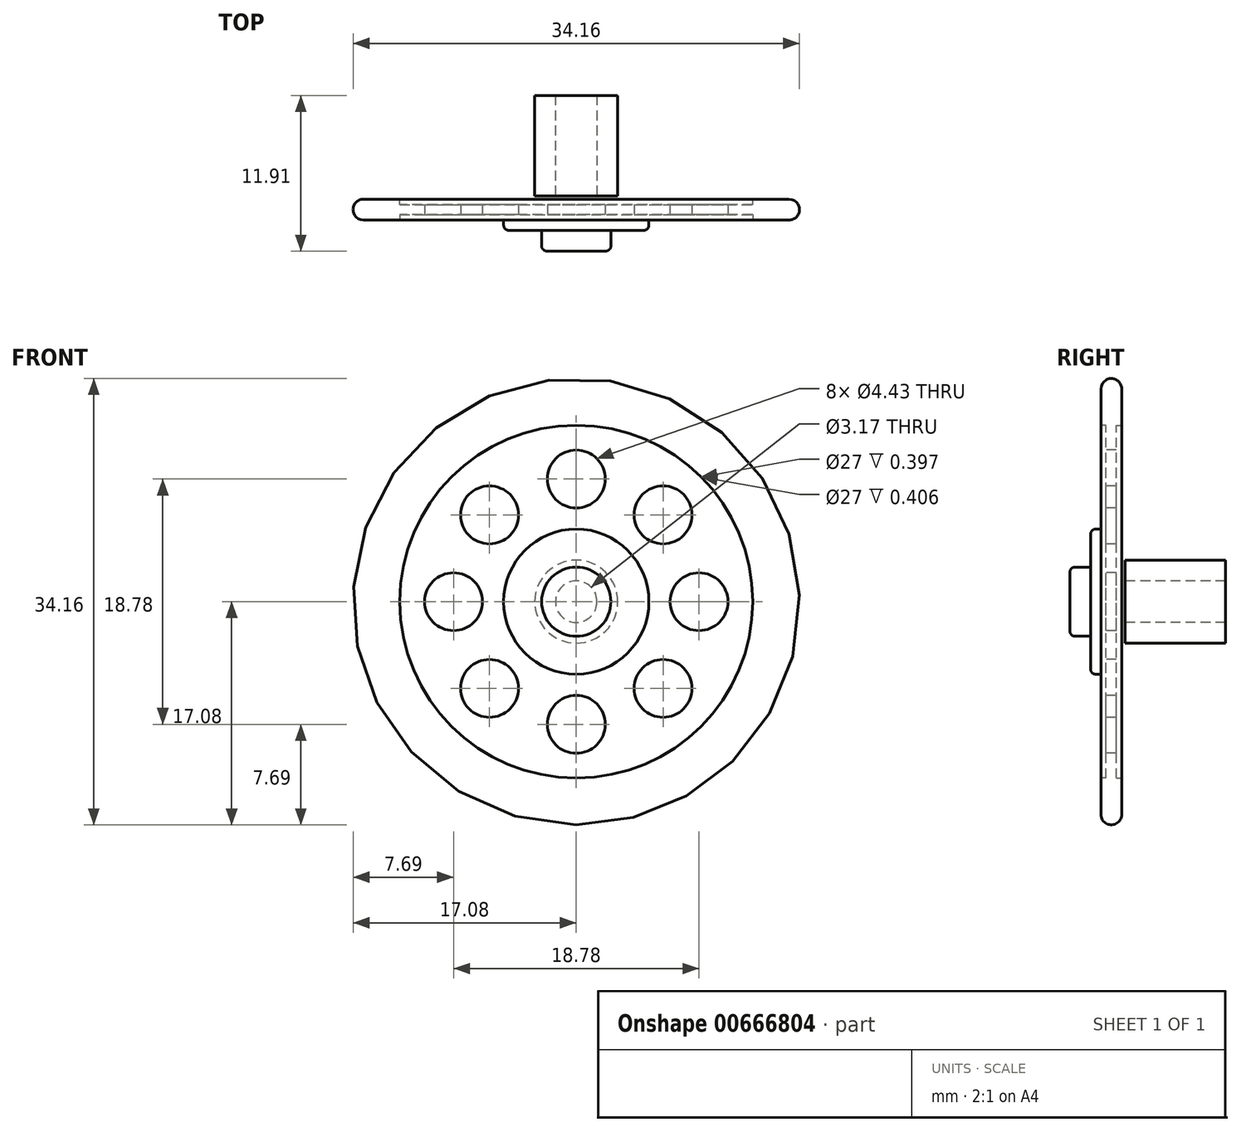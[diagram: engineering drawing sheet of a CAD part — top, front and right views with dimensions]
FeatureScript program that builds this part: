
annotation { "Feature Type Name" : "Feature", "Feature Type Description" : "" }
export const myFeature = defineFeature(function(context is Context, id is Id, definition is map)
    precondition{}
    {
        {
            var Q0;
            Q0=qCreatedBy(makeId("Front.planeOp"),FACE);
            var sketch = newSketch(context, id + "F0", { "sketchPlane" : qUnion([Q0])});
            skCircle(sketch, "E0", {"center": v(0, 0) * mm, "radius": 17.08 * mm});
            skSolve(sketch);
        }
        {
            var Q0;
            Q0=makeQuery(id+"F0.imprint","IMPRINT",FACE,{"disambiguationData":[TD([[makeQuery(id+"F0.imprint","IMPRINT",EDGE,{"derivedFrom":sQuery(id+"F0.wireOp",EDGE,"E0")}),1.0]])]});
            var sketch = newSketch(context, id + "F1", { "sketchPlane" : qUnion([Q0])});
            skSolve(sketch);
        }
        {
            var Q0;
            Q0=makeQuery(id+"F0.imprint","IMPRINT",FACE,{"disambiguationData":[TD([[makeQuery(id+"F0.imprint","IMPRINT",EDGE,{"derivedFrom":sQuery(id+"F0.wireOp",EDGE,"E0")}),1.0]])]});
            extrude(context, id + "F2", {"entities" : qUnion([Q0]), "depth" : 1.59 * mm, "offsetDistance" : 25.4 * mm});
        }
        {
            var Q0;
            Q0=makeQuery(id+"F2.opExtrude","CAP_FACE",FACE,{"disambiguationData":[OSD([sQuery(id+"F0.wireOp",EDGE,"E0")])],"isStart":false});
            var sketch = newSketch(context, id + "F3", { "sketchPlane" : qUnion([Q0])});
            skCircle(sketch, "E1", {"center": v(0, 0) * mm, "radius": 13.5 * mm});
            skCircle(sketch, "E2", {"center": v(0, 0) * mm, "radius": 5.56 * mm});
            skSolve(sketch);
        }
        {
            var Q0;
            Q0=makeQuery(id+"F3.imprint","IMPRINT",FACE,{"disambiguationData":[TD([[makeQuery(id+"F3.imprint","IMPRINT",EDGE,{"derivedFrom":sQuery(id+"F3.wireOp",EDGE,"E2")}),1.0]])]});
            extrude(context, id + "F4", {"entities" : qUnion([Q0]), "operationType" : NewBodyOperationType.ADD, "depth" : 0.8 * mm, "offsetDistance" : 25.4 * mm});
        }
        {
            var Q0;
            Q0=makeQuery(id+"F4.opExtrude","CAP_FACE",FACE,{"disambiguationData":[OSD([sQuery(id+"F3.wireOp",EDGE,"E2")])],"isStart":false});
            var sketch = newSketch(context, id + "F5", { "sketchPlane" : qUnion([Q0])});
            skCircle(sketch, "E3", {"center": v(0, 0) * mm, "radius": 2.65 * mm});
            skSolve(sketch);
        }
        {
            var Q0;
            Q0=makeQuery(id+"F5.imprint","IMPRINT",FACE,{"disambiguationData":[TD([[makeQuery(id+"F5.imprint","IMPRINT",EDGE,{"derivedFrom":sQuery(id+"F5.wireOp",EDGE,"E3")}),1.0]])]});
            extrude(context, id + "F6", {"entities" : qUnion([Q0]), "operationType" : NewBodyOperationType.ADD, "depth" : 1.59 * mm, "offsetDistance" : 25.4 * mm});
        }
        {
            var Q0;
            Q0=makeQuery(id+"F2.opExtrude","CAP_FACE",FACE,{"disambiguationData":[OSD([sQuery(id+"F0.wireOp",EDGE,"E0")])],"isStart":false});
            var sketch = newSketch(context, id + "F7", { "sketchPlane" : qUnion([Q0])});
            skSolve(sketch);
        }
        {
            var Q0;
            Q0=makeQuery(id+"F7.imprint","IMPRINT",FACE,{"disambiguationData":[TD([[makeQuery(id+"F7.imprint","IMPRINT",EDGE,{"derivedFrom":makeQuery(id+"F2.opExtrude","CAP_EDGE",EDGE,{"disambiguationData":[OSD([sQuery(id+"F0.wireOp",EDGE,"E0")])],"isStart":false})}),1.0]])]});
            var sketch = newSketch(context, id + "F8", { "sketchPlane" : qUnion([Q0])});
            skCircle(sketch, "E4", {"center": v(0, 0) * mm, "radius": 13.5 * mm});
            skSolve(sketch);
        }
        {
            var Q0;
            Q0 = qSketchRegion(id + "F8", true);
            extrude(context, id + "F9", {"entities" : qUnion([Q0]), "operationType" : NewBodyOperationType.REMOVE, "oppositeDirection" : true, "depth" : 0.4 * mm, "offsetDistance" : 25.4 * mm});
        }
        {
            var Q0;
            Q0=makeQuery(id+"F7.imprint","IMPRINT",FACE,{"disambiguationData":[TD([[makeQuery(id+"F7.imprint","IMPRINT",EDGE,{"derivedFrom":makeQuery(id+"F2.opExtrude","CAP_EDGE",EDGE,{"disambiguationData":[OSD([sQuery(id+"F0.wireOp",EDGE,"E0")])],"isStart":false})}),1.0]])]});
            var sketch = newSketch(context, id + "F10", { "sketchPlane" : qUnion([Q0])});
            skCircle(sketch, "E5", {"center": v(0, 0) * mm, "radius": 14.29 * mm});
            skSolve(sketch);
        }
        {
            var Q0;
            Q0=sQuery(id+"F10.wireOp",EDGE,"E5");
            extrude(context, id + "F11", {"bodyType" : ToolBodyType.SURFACE, "surfaceEntities" : qUnion([Q0]), "oppositeDirection" : true, "depth" : 0.25 * mm, "offsetDistance" : 25.4 * mm});
        }
        {
            var Q0;
            Q0=makeQuery(id+"F7.imprint","IMPRINT",FACE,{"disambiguationData":[TD([[makeQuery(id+"F7.imprint","IMPRINT",EDGE,{"derivedFrom":makeQuery(id+"F2.opExtrude","CAP_EDGE",EDGE,{"disambiguationData":[OSD([sQuery(id+"F0.wireOp",EDGE,"E0")])],"isStart":false})}),1.0]])]});
            var sketch = newSketch(context, id + "F12", { "sketchPlane" : qUnion([Q0])});
            skCircle(sketch, "E6", {"center": v(0, 9.39) * mm, "radius": 2.21 * mm});
            skCircle(sketch, "E7.1.0", {"center": v(-6.64, 6.64) * mm, "radius": 2.21 * mm});
            skCircle(sketch, "E7.2.0", {"center": v(-9.39, 0) * mm, "radius": 2.21 * mm});
            skCircle(sketch, "E7.3.0", {"center": v(-6.64, -6.64) * mm, "radius": 2.21 * mm});
            skCircle(sketch, "E7.4.0", {"center": v(0, -9.39) * mm, "radius": 2.21 * mm});
            skCircle(sketch, "E7.5.0", {"center": v(6.64, -6.64) * mm, "radius": 2.21 * mm});
            skCircle(sketch, "E7.6.0", {"center": v(9.39, 0) * mm, "radius": 2.21 * mm});
            skCircle(sketch, "E7.7.0", {"center": v(6.64, 6.64) * mm, "radius": 2.21 * mm});
            skPoint(sketch, "E7.center", {"position": v(0, 0) * mm});
            skSolve(sketch);
        }
        {
            var Q0;
            Q0=makeQuery(id+"F12.imprint","IMPRINT",FACE,{"disambiguationData":[TD([[makeQuery(id+"F12.imprint","IMPRINT",EDGE,{"derivedFrom":sQuery(id+"F12.wireOp",EDGE,"E6")}),1.0]])]});
            var Q1;
            Q1=makeQuery(id+"F12.imprint","IMPRINT",FACE,{"disambiguationData":[TD([[makeQuery(id+"F12.imprint","IMPRINT",EDGE,{"derivedFrom":sQuery(id+"F12.wireOp",EDGE,"E7.2.0")}),1.0]])]});
            var Q2;
            Q2=makeQuery(id+"F12.imprint","IMPRINT",FACE,{"disambiguationData":[TD([[makeQuery(id+"F12.imprint","IMPRINT",EDGE,{"derivedFrom":sQuery(id+"F12.wireOp",EDGE,"E7.1.0")}),1.0]])]});
            var Q3;
            Q3=makeQuery(id+"F12.imprint","IMPRINT",FACE,{"disambiguationData":[TD([[makeQuery(id+"F12.imprint","IMPRINT",EDGE,{"derivedFrom":sQuery(id+"F12.wireOp",EDGE,"E7.3.0")}),1.0]])]});
            var Q4;
            Q4=makeQuery(id+"F12.imprint","IMPRINT",FACE,{"disambiguationData":[TD([[makeQuery(id+"F12.imprint","IMPRINT",EDGE,{"derivedFrom":sQuery(id+"F12.wireOp",EDGE,"E7.7.0")}),1.0]])]});
            var Q5;
            Q5=makeQuery(id+"F12.imprint","IMPRINT",FACE,{"disambiguationData":[TD([[makeQuery(id+"F12.imprint","IMPRINT",EDGE,{"derivedFrom":sQuery(id+"F12.wireOp",EDGE,"E7.6.0")}),1.0]])]});
            var Q6;
            Q6=makeQuery(id+"F12.imprint","IMPRINT",FACE,{"disambiguationData":[TD([[makeQuery(id+"F12.imprint","IMPRINT",EDGE,{"derivedFrom":sQuery(id+"F12.wireOp",EDGE,"E7.5.0")}),1.0]])]});
            var Q7;
            Q7=makeQuery(id+"F12.imprint","IMPRINT",FACE,{"disambiguationData":[TD([[makeQuery(id+"F12.imprint","IMPRINT",EDGE,{"derivedFrom":sQuery(id+"F12.wireOp",EDGE,"E7.4.0")}),1.0]])]});
            extrude(context, id + "F13", {"entities" : qUnion([Q0, Q1, Q2, Q3, Q4, Q5, Q6, Q7]), "operationType" : NewBodyOperationType.REMOVE, "oppositeDirection" : true, "depth" : 203.2 * mm, "offsetDistance" : 25.4 * mm});
        }
        {
            var Q0;
            Q0=makeQuery(id+"F1.imprint","IMPRINT",FACE,{"disambiguationData":[TD([[makeQuery(id+"F1.imprint","IMPRINT",EDGE,{"derivedFrom":makeQuery(id+"F0.imprint","IMPRINT",EDGE,{"derivedFrom":sQuery(id+"F0.wireOp",EDGE,"E0")})}),1.0]])]});
            var sketch = newSketch(context, id + "F14", { "sketchPlane" : qUnion([Q0])});
            skCircle(sketch, "E8", {"center": v(0, 0) * mm, "radius": 3.18 * mm});
            skCircle(sketch, "E9", {"center": v(0, 0) * mm, "radius": 1.59 * mm});
            skSolve(sketch);
        }
        {
            var Q0;
            Q0=makeQuery(id+"F14.imprint","IMPRINT",FACE,{"disambiguationData":[TD([[makeQuery(id+"F14.imprint","IMPRINT",EDGE,{"derivedFrom":sQuery(id+"F14.wireOp",EDGE,"E8")}),1.0]])]});
            extrude(context, id + "F15", {"entities" : qUnion([Q0]), "operationType" : NewBodyOperationType.ADD, "oppositeDirection" : true, "depth" : 7.94 * mm, "offsetDistance" : 25.4 * mm});
        }
        {
            var Q0;
            Q0=makeQuery(id+"F2.opExtrude","CAP_EDGE",EDGE,{"disambiguationData":[OSD([sQuery(id+"F0.wireOp",EDGE,"E0")])],"isStart":true});
            var Q1;
            Q1=makeQuery(id+"F2.opExtrude","CAP_EDGE",EDGE,{"disambiguationData":[OSD([sQuery(id+"F0.wireOp",EDGE,"E0")])],"isStart":false});
            var Q2;
            Q2=makeQuery(id+"F15.opExtrude","CAP_EDGE",EDGE,{"disambiguationData":[OSD([sQuery(id+"F14.wireOp",EDGE,"E8")])],"isStart":true});
            fillet(context, id + "F16", {"entities" : qUnion([Q0, Q1, Q2]), "radius" : 0.8 * mm, "tangentPropagation" : true, "allowEdgeOverflow" : false});
        }
        {
            var Q0;
            Q0=makeQuery(id+"F6.opExtrude","CAP_EDGE",EDGE,{"disambiguationData":[OSD([sQuery(id+"F5.wireOp",EDGE,"E3")])],"isStart":false});
            var Q1;
            Q1=makeQuery(id+"F6.opExtrude","CAP_EDGE",EDGE,{"disambiguationData":[OSD([sQuery(id+"F5.wireOp",EDGE,"E3")])],"isStart":true});
            var Q2;
            Q2=makeQuery(id+"F4.opExtrude","CAP_EDGE",EDGE,{"disambiguationData":[OSD([sQuery(id+"F3.wireOp",EDGE,"E2")])],"isStart":false});
            fillet(context, id + "F17", {"entities" : qUnion([Q0, Q1, Q2]), "radius" : 0.4 * mm, "tangentPropagation" : true, "allowEdgeOverflow" : false});
        }
        {
            var Q0;
            Q0=makeQuery(id+"F1.imprint","IMPRINT",FACE,{"disambiguationData":[TD([[makeQuery(id+"F1.imprint","IMPRINT",EDGE,{"derivedFrom":makeQuery(id+"F0.imprint","IMPRINT",EDGE,{"derivedFrom":sQuery(id+"F0.wireOp",EDGE,"E0")})}),1.0]])]});
            var sketch = newSketch(context, id + "F18", { "sketchPlane" : qUnion([Q0])});
            skCircle(sketch, "E10", {"center": v(0, 0) * mm, "radius": 14.29 * mm});
            skCircle(sketch, "E11", {"center": v(0, 0) * mm, "radius": 13.5 * mm});
            skSolve(sketch);
        }
        {
            var Q0;
            Q0=makeQuery(id+"F18.imprint","IMPRINT",FACE,{"disambiguationData":[TD([[makeQuery(id+"F18.imprint","IMPRINT",EDGE,{"derivedFrom":sQuery(id+"F18.wireOp",EDGE,"E11")}),1.0]])]});
            extrude(context, id + "F19", {"entities" : qUnion([Q0]), "operationType" : NewBodyOperationType.REMOVE, "depth" : 0.4 * mm, "offsetDistance" : 25.4 * mm});
        }
        {
            var Q0;
            Q0=makeQuery(id+"F1.imprint","IMPRINT",FACE,{"disambiguationData":[TD([[makeQuery(id+"F1.imprint","IMPRINT",EDGE,{"derivedFrom":makeQuery(id+"F0.imprint","IMPRINT",EDGE,{"derivedFrom":sQuery(id+"F0.wireOp",EDGE,"E0")})}),1.0]])]});
            var sketch = newSketch(context, id + "F20", { "sketchPlane" : qUnion([Q0])});
            skCircle(sketch, "E12", {"center": v(0, 0) * mm, "radius": 14.29 * mm});
            skSolve(sketch);
        }
        {
            var Q0;
            Q0=makeQuery(id+"F20.imprint","IMPRINT",FACE,{"disambiguationData":[TD([[makeQuery(id+"F20.imprint","IMPRINT",EDGE,{"derivedFrom":sQuery(id+"F20.wireOp",EDGE,"E12")}),1.0]])]});
            extrude(context, id + "F21", {"entities" : qUnion([Q0]), "operationType" : NewBodyOperationType.REMOVE, "oppositeDirection" : true, "depth" : 0.25 * mm, "offsetDistance" : 25.4 * mm});
        }
    });
